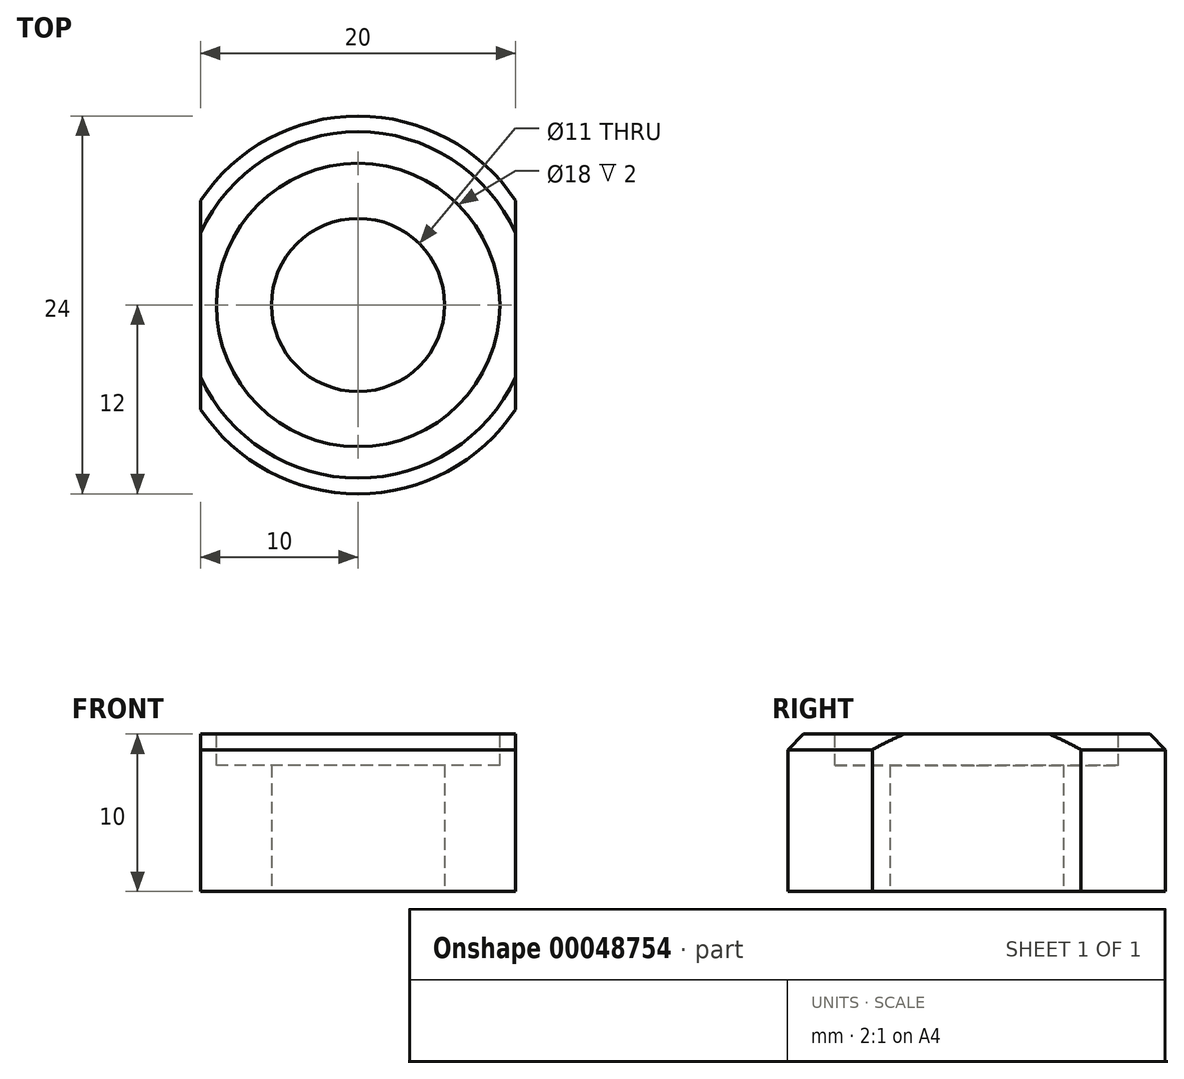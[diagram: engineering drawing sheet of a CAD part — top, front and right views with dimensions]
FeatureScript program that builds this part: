
annotation { "Feature Type Name" : "Feature", "Feature Type Description" : "" }
export const myFeature = defineFeature(function(context is Context, id is Id, definition is map)
    precondition{}
    {
        {
            var Q0;
            Q0=qCreatedBy(makeId("Top.planeOp"),FACE);
            var sketch = newSketch(context, id + "F0", { "sketchPlane" : qUnion([Q0])});
            skCircle(sketch, "E0", {"center": v(0, 0) * mm, "radius": 5.5 * mm});
            skCircle(sketch, "E1", {"center": v(0, 0) * mm, "radius": 12 * mm});
            skPoint(sketch, "E2", {"position": v(-10, 0) * mm});
            skLineSegment(sketch, "E3", {"start": v(-10, 6.63) * mm, "end": v(-10, -6.63) * mm});
            skLineSegment(sketch, "E4.MirrorCS", {"start": v(10, 6.63) * mm, "end": v(10, -6.63) * mm});
            skSolve(sketch);
        }
        {
            var Q0;
            Q0=makeQuery(id+"F0.imprint","IMPRINT",FACE,{"disambiguationData":[TD([[makeQuery(id+"F0.imprint","IMPRINT",EDGE,{"derivedFrom":sQuery(id+"F0.wireOp",EDGE,"E0")}),-1.0]])]});
            extrude(context, id + "F1", {"entities" : qUnion([Q0]), "depth" : 10 * mm});
        }
        {
            var Q0;
            Q0=makeQuery(id+"F1.opExtrude","CAP_FACE",FACE,{"disambiguationData":[OSD([sQuery(id+"F0.wireOp",EDGE,"E0"),sQuery(id+"F0.wireOp",EDGE,"E1")])],"isStart":false});
            var sketch = newSketch(context, id + "F2", { "sketchPlane" : qUnion([Q0])});
            skCircle(sketch, "E5", {"center": v(0, 0) * mm, "radius": 9 * mm});
            skSolve(sketch);
        }
        {
            var Q0;
            Q0=makeQuery(id+"F2.imprint","IMPRINT",FACE,{"disambiguationData":[TD([[makeQuery(id+"F2.imprint","IMPRINT",EDGE,{"derivedFrom":sQuery(id+"F2.wireOp",EDGE,"E5")}),1.0]])]});
            extrude(context, id + "F3", {"entities" : qUnion([Q0]), "operationType" : NewBodyOperationType.REMOVE, "oppositeDirection" : true, "depth" : 2 * mm});
        }
        {
            var Q0;
            Q0=makeQuery(id+"F1.opExtrude","CAP_EDGE",EDGE,{"disambiguationData":[OSD([sQuery(id+"F0.wireOp",EDGE,"E1")])],"isStart":false});
            chamfer(context, id + "F4", {"entities" : qUnion([Q0]), "width" : 1 * mm, "tangentPropagation" : true});
        }
    });
